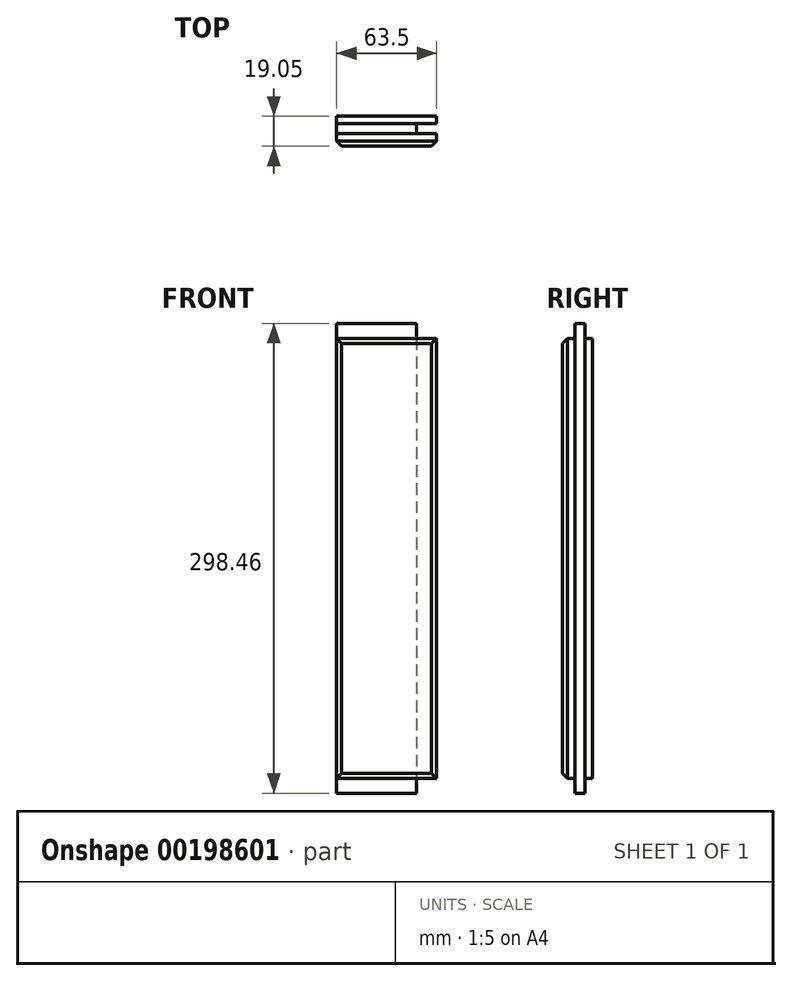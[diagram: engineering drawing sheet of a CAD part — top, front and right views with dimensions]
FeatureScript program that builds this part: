
annotation { "Feature Type Name" : "Feature", "Feature Type Description" : "" }
export const myFeature = defineFeature(function(context is Context, id is Id, definition is map)
    precondition{}
    {
        {
            var Q0;
            Q0=qCreatedBy(makeId("Top.planeOp"),FACE);
            var sketch = newSketch(context, id + "F0", { "sketchPlane" : qUnion([Q0])});
            skLineSegment(sketch, "E0.bottom", {"start": v(0, 0) * mm, "end": v(63.5, 0) * mm});
            skLineSegment(sketch, "E0.top", {"start": v(0, 19.05) * mm, "end": v(63.5, 19.05) * mm});
            skLineSegment(sketch, "E0.left", {"start": v(0, 0) * mm, "end": v(0, 19.05) * mm});
            skLineSegment(sketch, "E0.right", {"start": v(63.5, 0) * mm, "end": v(63.5, 19.05) * mm});
            skSolve(sketch);
        }
        {
            var Q0;
            Q0 = qSketchRegion(id + "F0", true);
            extrude(context, id + "F1", {"entities" : qUnion([Q0]), "depth" : 279.4 * mm});
        }
        {
            var Q0;
            Q0=makeQuery(id+"F1.opExtrude","SWEPT_EDGE",EDGE,{"disambiguationData":[OSD([sQuery(id+"F0.wireOp",EDGE,"E0.bottom"),sQuery(id+"F0.wireOp",EDGE,"E0.left")])]});
            var Q1;
            Q1=makeQuery(id+"F1.opExtrude","CAP_EDGE",EDGE,{"disambiguationData":[OSD([sQuery(id+"F0.wireOp",EDGE,"E0.bottom")])],"isStart":false});
            var Q2;
            Q2=makeQuery(id+"F1.opExtrude","SWEPT_EDGE",EDGE,{"disambiguationData":[OSD([sQuery(id+"F0.wireOp",EDGE,"E0.bottom"),sQuery(id+"F0.wireOp",EDGE,"E0.right")])]});
            var Q3;
            Q3=makeQuery(id+"F1.opExtrude","CAP_EDGE",EDGE,{"disambiguationData":[OSD([sQuery(id+"F0.wireOp",EDGE,"E0.bottom")])],"isStart":true});
            chamfer(context, id + "F2", {"entities" : qUnion([Q0, Q1, Q2, Q3]), "width" : 3.17 * mm, "tangentPropagation" : true});
        }
        {
            var Q0;
            Q0=makeQuery(id+"F1.opExtrude","CAP_FACE",FACE,{"disambiguationData":[OSD([sQuery(id+"F0.wireOp",EDGE,"E0.bottom"),sQuery(id+"F0.wireOp",EDGE,"E0.top"),sQuery(id+"F0.wireOp",EDGE,"E0.left"),sQuery(id+"F0.wireOp",EDGE,"E0.right")])],"isStart":true});
            var sketch = newSketch(context, id + "F3", { "sketchPlane" : qUnion([Q0])});
            skLineSegment(sketch, "E1", {"start": v(63.5, -14.29) * mm, "end": v(50.8, -14.29) * mm});
            skLineSegment(sketch, "E2", {"start": v(50.8, -14.29) * mm, "end": v(50.8, -7.94) * mm});
            skLineSegment(sketch, "E3", {"start": v(50.8, -7.94) * mm, "end": v(63.5, -7.94) * mm});
            skLineSegment(sketch, "E4", {"start": v(63.5, -7.94) * mm, "end": v(63.5, -14.29) * mm});
            skSolve(sketch);
        }
        {
            var Q0;
            Q0 = qSketchRegion(id + "F3", true);
            extrude(context, id + "F4", {"entities" : qUnion([Q0]), "operationType" : NewBodyOperationType.REMOVE, "endBound" : BoundingType.THROUGH_ALL, "oppositeDirection" : true, "depth" : 25.4 * mm});
        }
        {
            var Q0;
            Q0=makeQuery(id+"F1.opExtrude","SWEPT_FACE",FACE,{"disambiguationData":[OSD([sQuery(id+"F0.wireOp",EDGE,"E0.left")])]});
            var sketch = newSketch(context, id + "F5", { "sketchPlane" : qUnion([Q0])});
            skLineSegment(sketch, "E5", {"start": v(-14.29, 279.4) * mm, "end": v(-14.29, 288.93) * mm});
            skLineSegment(sketch, "E6", {"start": v(-14.29, 288.93) * mm, "end": v(-7.94, 288.93) * mm});
            skLineSegment(sketch, "E7", {"start": v(-7.94, 288.93) * mm, "end": v(-7.94, 279.4) * mm});
            skLineSegment(sketch, "E8", {"start": v(-7.94, 279.4) * mm, "end": v(-14.29, 279.4) * mm});
            skLineSegment(sketch, "E9", {"start": v(-14.29, 0) * mm, "end": v(-14.29, -9.53) * mm});
            skLineSegment(sketch, "E10", {"start": v(-14.29, -9.53) * mm, "end": v(-7.94, -9.53) * mm});
            skLineSegment(sketch, "E11", {"start": v(-7.94, -9.53) * mm, "end": v(-7.94, 0) * mm});
            skLineSegment(sketch, "E12", {"start": v(-7.94, 0) * mm, "end": v(-14.29, 0) * mm});
            skSolve(sketch);
        }
        {
            var Q0;
            Q0 = qSketchRegion(id + "F5", true);
            extrude(context, id + "F6", {"entities" : qUnion([Q0]), "operationType" : NewBodyOperationType.ADD, "oppositeDirection" : true, "depth" : 50.8 * mm});
        }
    });
